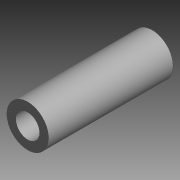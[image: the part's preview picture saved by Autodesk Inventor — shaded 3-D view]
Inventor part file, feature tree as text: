
AUTODESK INVENTOR PART (.ipt)
format: ipt  version: 2014 SP1 (Build 180222100, 222)  size: 81,408 bytes
history: native  units: in
note: dims shown in document units (in); Inventor stores cm internally (conversion verified against a paired STEP export)
features: extrude x1, chamfer x1, sketch x1
ambient origin geometry x8: Origin, YZ Plane, XZ Plane, XY Plane, X Axis, Y Axis, Z Axis, Center Point
bodies: Solid1 (feature_tree)
feature tree (3):
  extrude  "Extrusion1"  Depth=0.748in
  chamfer  "Chamfer1"  Distance=0.748in
  sketch  "Sketch1"  dims[d0=0.25in d1=0.1437in d2=0.748in d3=0.0in d4=0.0197in d5=0.0787in d6=45.0deg]
